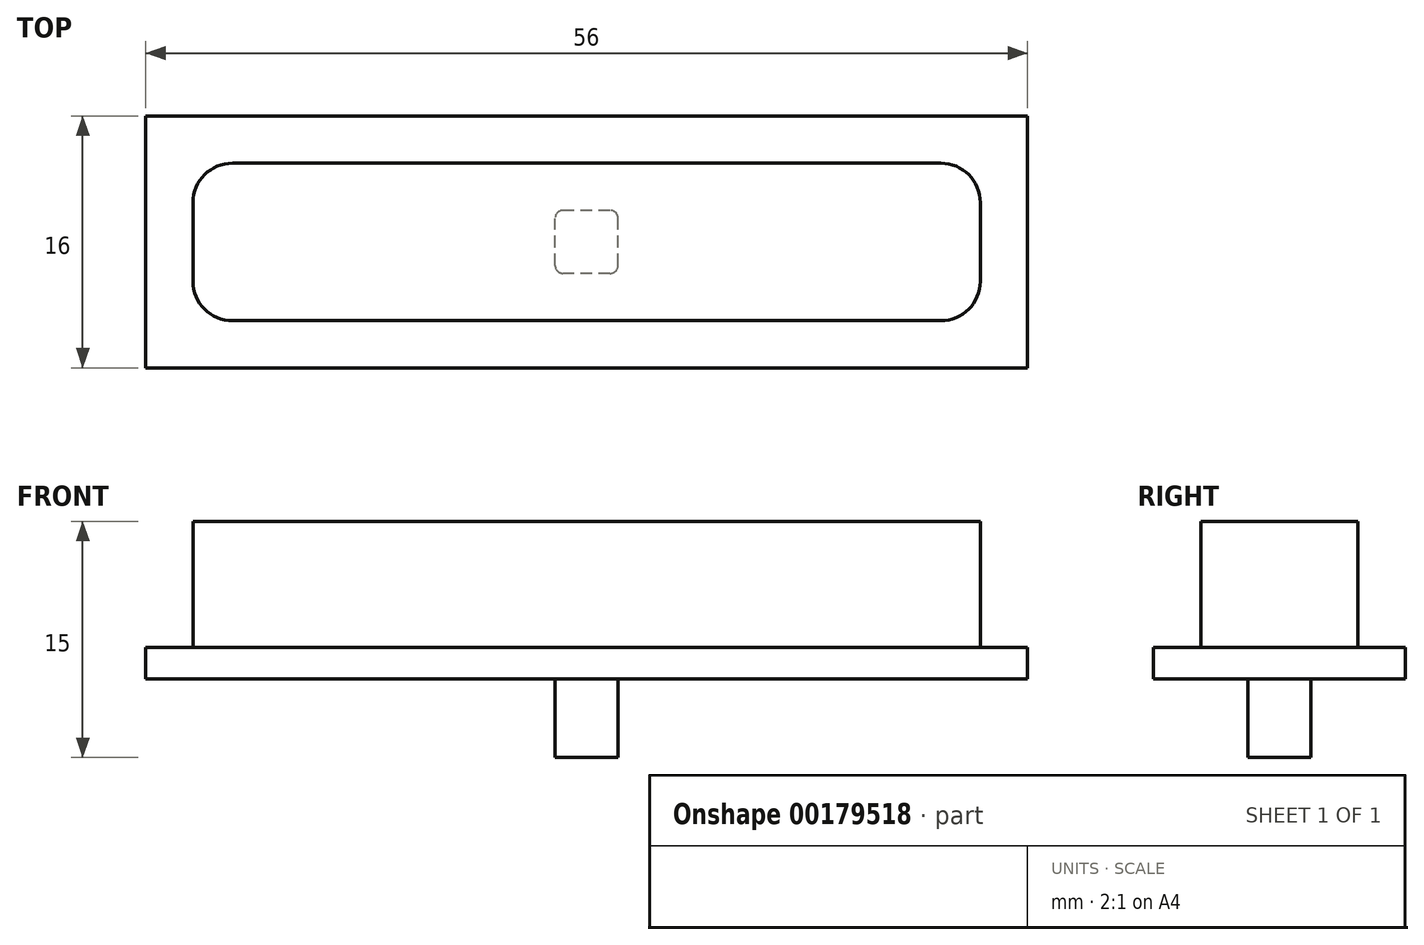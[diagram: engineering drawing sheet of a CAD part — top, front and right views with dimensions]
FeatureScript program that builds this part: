
annotation { "Feature Type Name" : "Feature", "Feature Type Description" : "" }
export const myFeature = defineFeature(function(context is Context, id is Id, definition is map)
    precondition{}
    {
        {
            var Q0;
            Q0=qCreatedBy(makeId("Top.planeOp"),FACE);
            var sketch = newSketch(context, id + "F0", { "sketchPlane" : qUnion([Q0])});
            skLineSegment(sketch, "E0.bottom", {"start": v(25, -5) * mm, "end": v(-25, -5) * mm});
            skLineSegment(sketch, "E0.top", {"start": v(25, 5) * mm, "end": v(-25, 5) * mm});
            skLineSegment(sketch, "E0.left", {"start": v(25, -5) * mm, "end": v(25, 5) * mm});
            skLineSegment(sketch, "E0.right", {"start": v(-25, -5) * mm, "end": v(-25, 5) * mm});
            skPoint(sketch, "E0.middle", {"position": v(0, 0) * mm});
            skLineSegment(sketch, "E1.bottom", {"start": v(2, -2) * mm, "end": v(-2, -2) * mm});
            skLineSegment(sketch, "E1.top", {"start": v(2, 2) * mm, "end": v(-2, 2) * mm});
            skLineSegment(sketch, "E1.left", {"start": v(2, -2) * mm, "end": v(2, 2) * mm});
            skLineSegment(sketch, "E1.right", {"start": v(-2, -2) * mm, "end": v(-2, 2) * mm});
            skCircle(sketch, "E2", {"center": v(0, 0) * mm, "radius": 1.6 * mm});
            skLineSegment(sketch, "E3.bottom", {"start": v(28, -8) * mm, "end": v(-28, -8) * mm});
            skLineSegment(sketch, "E3.top", {"start": v(28, 8) * mm, "end": v(-28, 8) * mm});
            skLineSegment(sketch, "E3.left", {"start": v(28, -8) * mm, "end": v(28, 8) * mm});
            skLineSegment(sketch, "E3.right", {"start": v(-28, -8) * mm, "end": v(-28, 8) * mm});
            skSolve(sketch);
        }
        {
            var Q0;
            Q0=makeQuery(id+"F0.imprint","IMPRINT",FACE,{"disambiguationData":[TD([[makeQuery(id+"F0.imprint","IMPRINT",EDGE,{"derivedFrom":sQuery(id+"F0.wireOp",EDGE,"E0.bottom")}),-1.0]])]});
            var Q1;
            Q1=makeQuery(id+"F0.imprint","IMPRINT",FACE,{"disambiguationData":[TD([[makeQuery(id+"F0.imprint","IMPRINT",EDGE,{"derivedFrom":sQuery(id+"F0.wireOp",EDGE,"E2")}),1.0]])]});
            var Q2;
            Q2=makeQuery(id+"F0.imprint","IMPRINT",FACE,{"disambiguationData":[TD([[makeQuery(id+"F0.imprint","IMPRINT",EDGE,{"derivedFrom":sQuery(id+"F0.wireOp",EDGE,"E1.bottom")}),-1.0]])]});
            extrude(context, id + "F1", {"entities" : qUnion([Q0, Q1, Q2]), "depth" : 10 * mm});
        }
        {
            var Q0;
            Q0=makeQuery(id+"F1.opExtrude","SWEPT_EDGE",EDGE,{"disambiguationData":[OSD([sQuery(id+"F0.wireOp",EDGE,"E0.bottom"),sQuery(id+"F0.wireOp",EDGE,"E0.right")])]});
            var Q1;
            Q1=makeQuery(id+"F1.opExtrude","SWEPT_EDGE",EDGE,{"disambiguationData":[OSD([sQuery(id+"F0.wireOp",EDGE,"E0.top"),sQuery(id+"F0.wireOp",EDGE,"E0.right")])]});
            var Q2;
            Q2=makeQuery(id+"F1.opExtrude","SWEPT_EDGE",EDGE,{"disambiguationData":[OSD([sQuery(id+"F0.wireOp",EDGE,"E0.bottom"),sQuery(id+"F0.wireOp",EDGE,"E0.left")])]});
            var Q3;
            Q3=makeQuery(id+"F1.opExtrude","SWEPT_EDGE",EDGE,{"disambiguationData":[OSD([sQuery(id+"F0.wireOp",EDGE,"E0.top"),sQuery(id+"F0.wireOp",EDGE,"E0.left")])]});
            fillet(context, id + "F2", {"entities" : qUnion([Q0, Q1, Q2, Q3]), "radius" : 2.5 * mm, "tangentPropagation" : true, "allowEdgeOverflow" : false});
        }
        {
            var Q0;
            Q0=makeQuery(id+"F0.imprint","IMPRINT",FACE,{"disambiguationData":[TD([[makeQuery(id+"F0.imprint","IMPRINT",EDGE,{"derivedFrom":sQuery(id+"F0.wireOp",EDGE,"E0.bottom")}),1.0]])]});
            extrude(context, id + "F3", {"entities" : qUnion([Q0]), "operationType" : NewBodyOperationType.ADD, "depth" : 2 * mm});
        }
        {
            var Q0;
            Q0=makeQuery(id+"F0.imprint","IMPRINT",FACE,{"disambiguationData":[TD([[makeQuery(id+"F0.imprint","IMPRINT",EDGE,{"derivedFrom":sQuery(id+"F0.wireOp",EDGE,"E0.bottom")}),-1.0]])]});
            extrude(context, id + "F4", {"entities" : qUnion([Q0]), "operationType" : NewBodyOperationType.ADD, "depth" : 2 * mm});
        }
        {
            var Q0;
            Q0=makeQuery(id+"F0.imprint","IMPRINT",FACE,{"disambiguationData":[TD([[makeQuery(id+"F0.imprint","IMPRINT",EDGE,{"derivedFrom":sQuery(id+"F0.wireOp",EDGE,"E1.bottom")}),-1.0]])]});
            var Q1;
            Q1=makeQuery(id+"F0.imprint","IMPRINT",FACE,{"disambiguationData":[TD([[makeQuery(id+"F0.imprint","IMPRINT",EDGE,{"derivedFrom":sQuery(id+"F0.wireOp",EDGE,"E2")}),1.0]])]});
            extrude(context, id + "F5", {"entities" : qUnion([Q0, Q1]), "operationType" : NewBodyOperationType.ADD, "oppositeDirection" : true, "depth" : 5 * mm});
        }
        {
            var Q0;
            Q0=sQuery(id+"F0.wireOp",EDGE,"E2");
            extrude(context, id + "F6", {"bodyType" : ToolBodyType.SURFACE, "surfaceEntities" : qUnion([Q0]), "oppositeDirection" : true, "depth" : 7 * mm});
        }
        {
            var Q0;
            Q0=makeQuery(id+"F5.opExtrude","SWEPT_EDGE",EDGE,{"disambiguationData":[OSD([sQuery(id+"F0.wireOp",EDGE,"E1.bottom"),sQuery(id+"F0.wireOp",EDGE,"E1.right")])]});
            var Q1;
            Q1=makeQuery(id+"F5.opExtrude","SWEPT_EDGE",EDGE,{"disambiguationData":[OSD([sQuery(id+"F0.wireOp",EDGE,"E1.bottom"),sQuery(id+"F0.wireOp",EDGE,"E1.left")])]});
            var Q2;
            Q2=makeQuery(id+"F5.opExtrude","SWEPT_EDGE",EDGE,{"disambiguationData":[OSD([sQuery(id+"F0.wireOp",EDGE,"E1.top"),sQuery(id+"F0.wireOp",EDGE,"E1.right")])]});
            var Q3;
            Q3=makeQuery(id+"F5.opExtrude","SWEPT_EDGE",EDGE,{"disambiguationData":[OSD([sQuery(id+"F0.wireOp",EDGE,"E1.top"),sQuery(id+"F0.wireOp",EDGE,"E1.left")])]});
            fillet(context, id + "F7", {"entities" : qUnion([Q0, Q1, Q2, Q3]), "radius" : 0.5 * mm, "tangentPropagation" : true, "allowEdgeOverflow" : false});
        }
    });
